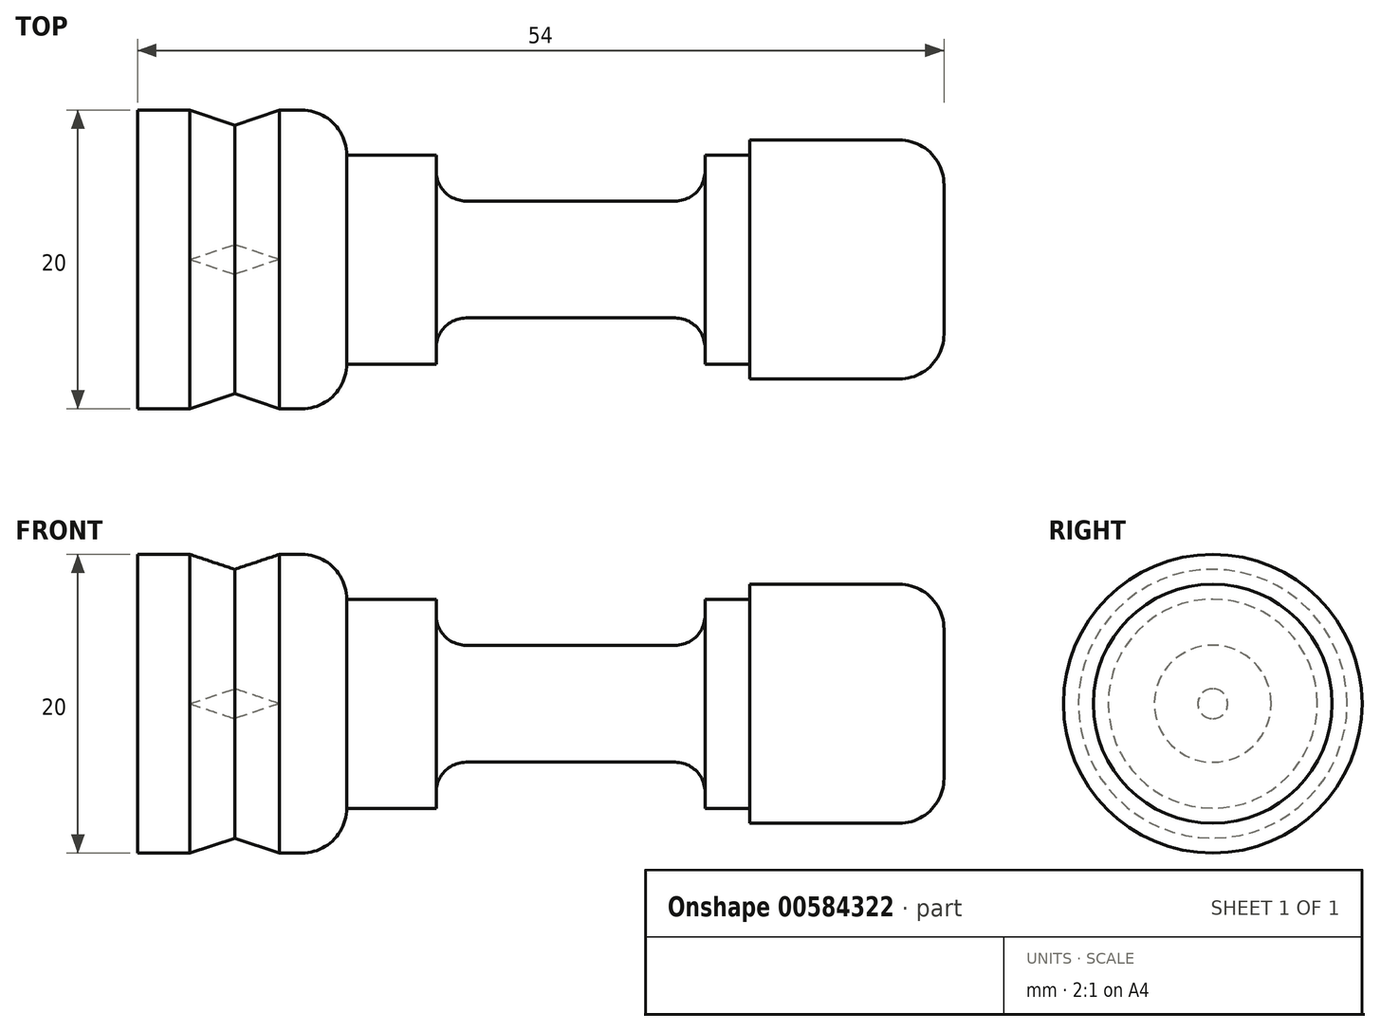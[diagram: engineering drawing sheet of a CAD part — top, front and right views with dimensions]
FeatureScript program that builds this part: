
annotation { "Feature Type Name" : "Feature", "Feature Type Description" : "" }
export const myFeature = defineFeature(function(context is Context, id is Id, definition is map)
    precondition{}
    {
        {
            var Q0;
            Q0=qCreatedBy(makeId("Front.planeOp"),FACE);
            var sketch = newSketch(context, id + "F0", { "sketchPlane" : qUnion([Q0])});
            skLineSegment(sketch, "E0", {"start": v(0, 0) * mm, "end": v(0, 10) * mm});
            skLineSegment(sketch, "E1", {"start": v(0, 0) * mm, "end": v(3.5, 0) * mm});
            skLineSegment(sketch, "E2", {"start": v(3.5, 10) * mm, "end": v(0, 10) * mm});
            skLineSegment(sketch, "E3", {"start": v(9.5, 10) * mm, "end": v(14, 10) * mm});
            skLineSegment(sketch, "E4", {"start": v(3.5, 0) * mm, "end": v(6.5, 1) * mm});
            skLineSegment(sketch, "E5", {"start": v(3.5, 10) * mm, "end": v(6.5, 9) * mm});
            skLineSegment(sketch, "E6", {"start": v(6.5, 9) * mm, "end": v(9.5, 10) * mm});
            skLineSegment(sketch, "E7", {"start": v(9.5, 0) * mm, "end": v(6.5, 1) * mm});
            skLineSegment(sketch, "E8", {"start": v(9.5, 0) * mm, "end": v(11, 0) * mm});
            skLineSegment(sketch, "E9.filletArc", {"start": v(14, 10) * mm, "end": v(14, 10) * mm});
            skArc(sketch, "E10.filletArc", {"start": v(11, 0) * mm, "mid": v(13.12, 0.88) * mm, "end": v(14, 3) * mm});
            skLineSegment(sketch, "E11", {"start": v(14, 10) * mm, "end": v(20, 10) * mm});
            skLineSegment(sketch, "E12", {"start": v(20, 3) * mm, "end": v(14, 3) * mm});
            skLineSegment(sketch, "E13", {"start": v(20, 10) * mm, "end": v(38, 10) * mm});
            skLineSegment(sketch, "E14", {"start": v(38, 4.08) * mm, "end": v(38, 3) * mm});
            skLineSegment(sketch, "E15.bottom", {"start": v(20, 3) * mm, "end": v(20, 3) * mm});
            skLineSegment(sketch, "E16", {"start": v(20, 3) * mm, "end": v(20, 4.08) * mm});
            skLineSegment(sketch, "E17", {"start": v(22, 6.08) * mm, "end": v(36, 6.08) * mm});
            skArc(sketch, "E18.filletArc", {"start": v(22, 6.08) * mm, "mid": v(20.59, 5.5) * mm, "end": v(20, 4.08) * mm});
            skArc(sketch, "E19.filletArc", {"start": v(38, 4.08) * mm, "mid": v(37.41, 5.5) * mm, "end": v(36, 6.08) * mm});
            skLineSegment(sketch, "E20", {"start": v(38, 3) * mm, "end": v(41, 3) * mm});
            skLineSegment(sketch, "E21", {"start": v(41, 10) * mm, "end": v(38, 10) * mm});
            skLineSegment(sketch, "E22", {"start": v(41, 3) * mm, "end": v(41, 2) * mm});
            skLineSegment(sketch, "E23", {"start": v(41, 2) * mm, "end": v(51, 2) * mm});
            skLineSegment(sketch, "E24", {"start": v(54, 5) * mm, "end": v(54, 10) * mm});
            skLineSegment(sketch, "E25", {"start": v(54, 10) * mm, "end": v(41, 10) * mm});
            skArc(sketch, "E26.filletArc", {"start": v(51, 2) * mm, "mid": v(53.12, 2.88) * mm, "end": v(54, 5) * mm});
            skLineSegment(sketch, "E27", {"start": v(-5.83, 10) * mm, "end": v(58.67, 10) * mm, "construction": true});
            skSolve(sketch);
        }
        {
            var Q0;
            Q0=makeQuery(id+"F0.imprint","IMPRINT",FACE,{"disambiguationData":[TD([[makeQuery(id+"F0.imprint","IMPRINT",EDGE,{"derivedFrom":sQuery(id+"F0.wireOp",EDGE,"E0")}),-1.0]])]});
            var Q1;
            Q1=sQuery(id+"F0.wireOp",EDGE,"E27");
            revolve(context, id + "F1", {"entities" : qUnion([Q0]), "axis" : qUnion([Q1]), "revolveType" : RevolveType.FULL});
        }
    });
